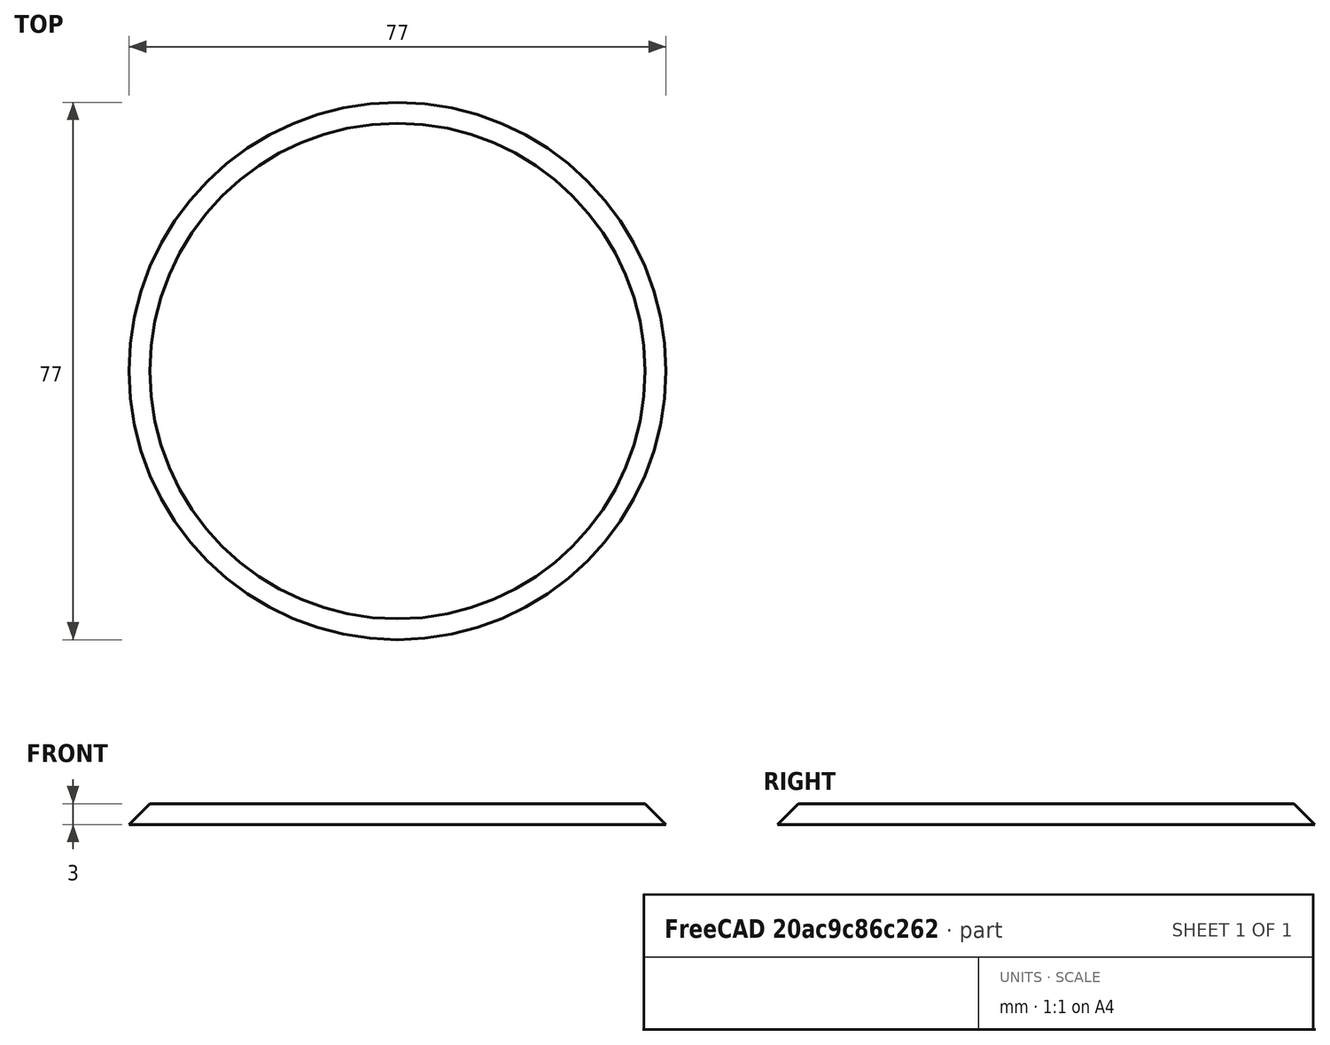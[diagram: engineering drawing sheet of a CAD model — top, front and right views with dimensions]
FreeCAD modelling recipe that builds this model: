
FCSTD DOCUMENT  (FreeCAD 0.21R33771 (Git))
Label: 炬为电子负载-顶部防尘盖
License: All rights reserved
LicenseURL: https://en.wikipedia.org/wiki/All_rights_reserved
objects: Sketcher::SketchObject×1, PartDesign::Pad×1, PartDesign::Chamfer×1, PartDesign::Body×1
note: 6 computed .brp shape members not serialized (recipe doc carries the construction recipe); baked Part::Feature solids carry a one-line shape summary decoded from their .brp

FEATURE [Sketcher::SketchObject] Sketch
  FullyConstrained = true
  MapMode = 5
  Support = -> [XY_Plane]
  sketch-geometry (1):
    g0: Circle CenterX=0 CenterY=0 CenterZ=0 NormalX=0 NormalY=0 NormalZ=1 AngleXU=0 Radius=38.5
  constraints (2):
    c: Coincident(g0,g-1)
    c: Diameter(g0) = 77
FEATURE [PartDesign::Pad] Pad
  Direction = (0,0,1)
  Length = 3
  Length2 = 10
  Profile = -> Sketch
  ReferenceAxis = -> Sketch [N_Axis]
  Type = 0
FEATURE [PartDesign::Chamfer] Chamfer
  Angle = 45
  Base = -> Pad [Edge3]
  BaseFeature = -> Pad
  ChamferType = 0
  FlipDirection = false
  Size = 2.99
  Size2 = 1
  SupportTransform = false
  UseAllEdges = false
FEATURE [PartDesign::Body] Body
  Group = -> [Sketch,Pad,Chamfer]
  Origin = -> Origin
  Tip = -> Chamfer
